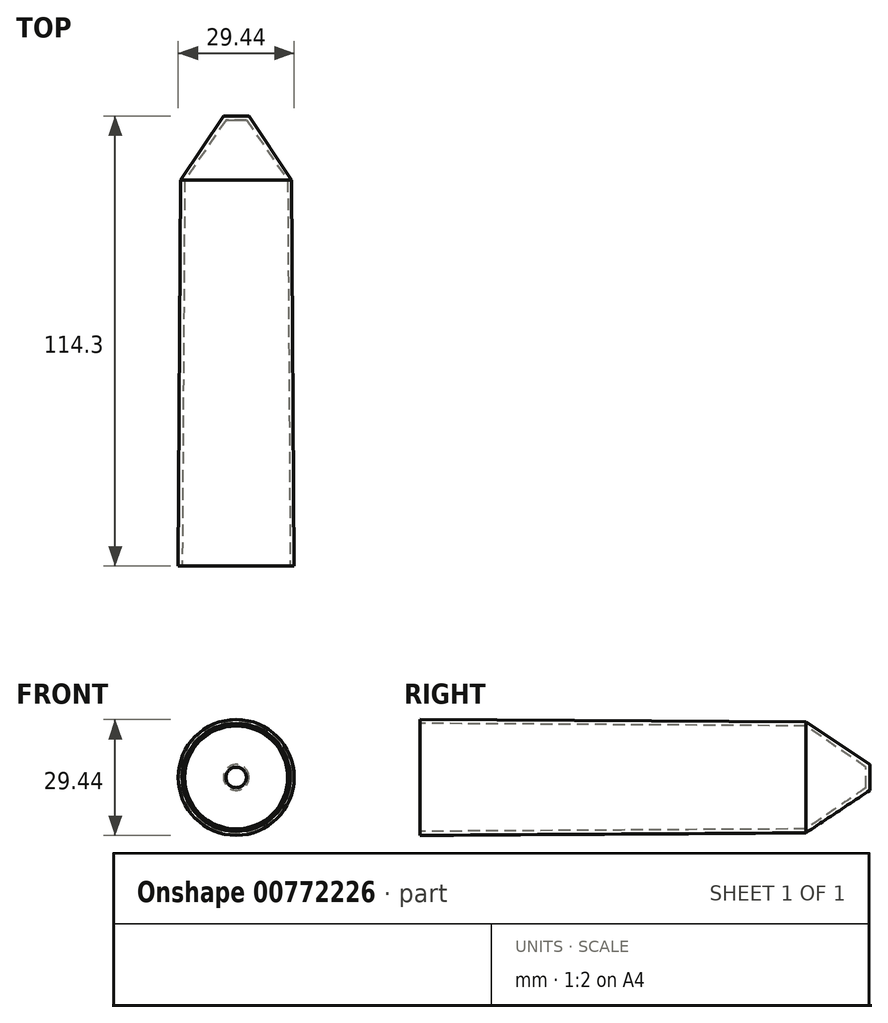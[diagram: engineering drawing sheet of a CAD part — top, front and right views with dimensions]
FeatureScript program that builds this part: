
annotation { "Feature Type Name" : "Feature", "Feature Type Description" : "" }
export const myFeature = defineFeature(function(context is Context, id is Id, definition is map)
    precondition{}
    {
        {
            var Q0;
            Q0=qCreatedBy(makeId("Front.planeOp"),FACE);
            var sketch = newSketch(context, id + "F0", { "sketchPlane" : qUnion([Q0])});
            skCircle(sketch, "E0", {"center": v(0, 0) * mm, "radius": 14.72 * mm});
            skSolve(sketch);
        }
        {
            var Q0;
            Q0=qCreatedBy(makeId("Front.planeOp"),FACE);
            cPlane(context, id + "F1", {"entities" : qUnion([Q0]), "cplaneType" : CPlaneType.OFFSET, "offset" : 98 * mm, "oppositeDirection" : true, "width" : 150 * mm, "height" : 150 * mm});
        }
        {
            var Q0;
            Q0=qCreatedBy(id+"F1.planeOp",FACE);
            var sketch = newSketch(context, id + "F2", { "sketchPlane" : qUnion([Q0])});
            skCircle(sketch, "E1", {"center": v(0, 0) * mm, "radius": 14.1 * mm});
            skSolve(sketch);
        }
        {
            var Q0;
            Q0=makeQuery(id+"F2.imprint","IMPRINT",FACE,{"disambiguationData":[TD([[makeQuery(id+"F2.imprint","IMPRINT",EDGE,{"derivedFrom":sQuery(id+"F2.wireOp",EDGE,"E1")}),1.0]])]});
            var Q1;
            Q1=makeQuery(id+"F0.imprint","IMPRINT",FACE,{"disambiguationData":[TD([[makeQuery(id+"F0.imprint","IMPRINT",EDGE,{"derivedFrom":sQuery(id+"F0.wireOp",EDGE,"E0")}),1.0]])]});
            loft(context, id + "F3", {"sheetProfilesArray" : [{ "sheetProfileEntities" : qUnion([Q0]) }, { "sheetProfileEntities" : qUnion([Q1]) }]});
        }
        {
            var Q0;
            Q0=qCreatedBy(makeId("Front.planeOp"),FACE);
            var sketch = newSketch(context, id + "F4", { "sketchPlane" : qUnion([Q0])});
            skCircle(sketch, "E2", {"center": v(0, 0) * mm, "radius": 13.72 * mm});
            skSolve(sketch);
        }
        {
            var Q0;
            Q0=qCreatedBy(id+"F1.planeOp",FACE);
            var sketch = newSketch(context, id + "F5", { "sketchPlane" : qUnion([Q0])});
            skCircle(sketch, "E3", {"center": v(0, 0) * mm, "radius": 13.1 * mm});
            skSolve(sketch);
        }
        {
            var Q0;
            Q0=qCreatedBy(id+"F1.planeOp",FACE);
            cPlane(context, id + "F6", {"entities" : qUnion([Q0]), "cplaneType" : CPlaneType.OFFSET, "offset" : 16.3 * mm, "oppositeDirection" : true, "width" : 150 * mm, "height" : 150 * mm});
        }
        {
            var Q0;
            Q0=qCreatedBy(id+"F6.planeOp",FACE);
            var sketch = newSketch(context, id + "F7", { "sketchPlane" : qUnion([Q0])});
            skCircle(sketch, "E4", {"center": v(0, 0) * mm, "radius": 3.27 * mm});
            skSolve(sketch);
        }
        {
            var Q0;
            Q0=qCreatedBy(id+"F6.planeOp",FACE);
            cPlane(context, id + "F8", {"entities" : qUnion([Q0]), "cplaneType" : CPlaneType.OFFSET, "offset" : 1 * mm, "width" : 150 * mm, "height" : 150 * mm});
        }
        {
            var Q1;
            Q1=makeQuery(id+"F3.opLoft","CAP_FACE",FACE,{"disambiguationData":[OSD([makeQuery(id+"F2.imprint","IMPRINT",FACE,{"disambiguationData":[TD([[makeQuery(id+"F2.imprint","IMPRINT",EDGE,{"derivedFrom":sQuery(id+"F2.wireOp",EDGE,"E1")}),1.0]])]})])],"isStart":true});
            var Q2;
            Q2=makeQuery(id+"F7.imprint","IMPRINT",FACE,{"disambiguationData":[TD([[makeQuery(id+"F7.imprint","IMPRINT",EDGE,{"derivedFrom":sQuery(id+"F7.wireOp",EDGE,"E4")}),1.0]])]});
            loft(context, id + "F9", {"operationType" : NewBodyOperationType.ADD, "sheetProfilesArray" : [{ "sheetProfileEntities" : qUnion([Q1]) }, { "sheetProfileEntities" : qUnion([Q2]) }]});
        }
        {
            var Q1;
            Q1=makeQuery(id+"F4.imprint","IMPRINT",FACE,{"disambiguationData":[TD([[makeQuery(id+"F4.imprint","IMPRINT",EDGE,{"derivedFrom":sQuery(id+"F4.wireOp",EDGE,"E2")}),1.0]])]});
            var Q2;
            Q2=makeQuery(id+"F5.imprint","IMPRINT",FACE,{"disambiguationData":[TD([[makeQuery(id+"F5.imprint","IMPRINT",EDGE,{"derivedFrom":sQuery(id+"F5.wireOp",EDGE,"E3")}),1.0]])]});
            loft(context, id + "F10", {"operationType" : NewBodyOperationType.REMOVE, "sheetProfilesArray" : [{ "sheetProfileEntities" : qUnion([Q1]) }, { "sheetProfileEntities" : qUnion([Q2]) }]});
        }
        {
            var Q0;
            Q0=qCreatedBy(id+"F8.planeOp",FACE);
            var sketch = newSketch(context, id + "F11", { "sketchPlane" : qUnion([Q0])});
            skCircle(sketch, "E5", {"center": v(0, 0) * mm, "radius": 2.6 * mm});
            skSolve(sketch);
        }
        {
            var Q1;
            Q1=makeQuery(id+"F10.boolean.opBoolean","COPY",FACE,{"derivedFrom":makeQuery(id+"F10.opLoft","CAP_FACE",FACE,{"disambiguationData":[OSD([makeQuery(id+"F5.imprint","IMPRINT",FACE,{"disambiguationData":[TD([[makeQuery(id+"F5.imprint","IMPRINT",EDGE,{"derivedFrom":sQuery(id+"F5.wireOp",EDGE,"E3")}),1.0]])]})])],"isStart":true})});
            var Q2;
            Q2=makeQuery(id+"F11.imprint","IMPRINT",FACE,{"disambiguationData":[TD([[makeQuery(id+"F11.imprint","IMPRINT",EDGE,{"derivedFrom":sQuery(id+"F11.wireOp",EDGE,"E5")}),1.0]])]});
            loft(context, id + "F12", {"operationType" : NewBodyOperationType.REMOVE, "sheetProfilesArray" : [{ "sheetProfileEntities" : qUnion([Q1]) }, { "sheetProfileEntities" : qUnion([Q2]) }]});
        }
    });
